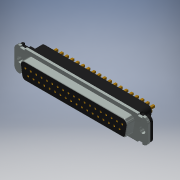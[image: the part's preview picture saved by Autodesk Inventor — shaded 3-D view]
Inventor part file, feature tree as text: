
AUTODESK INVENTOR PART (.ipt)
format: ipt  version: 2019 (Build 230136000, 136)  size: 427,520 bytes
history: native  units: mm (DEFAULTED — no unit token found)
features: extrude x12, pattern_linear x6, sketch x4, fillet x4, chamfer x1
ambient origin geometry x8: Origin, YZ Plane, XZ Plane, XY Plane, X Axis, Y Axis, Z Axis, Center Point
bodies: Solid1 (feature_tree)
feature tree (27):
  sketch  "Sketch1"  dims[d0=1.745329mm d6=0.381mm d7=2.418418mm d8=0.855895mm d9=2.418418mm]
  extrude  "Extrusion1"  Depth=0.381mm
  extrude  "Extrusion2"  Depth=1.314425mm
  fillet  "Fillet4"  Radius=1.397mm
  extrude  "Pin1"  Depth=5.08mm TaperAngle=0.0deg
  extrude  "Pin2"  Depth=5.08mm TaperAngle=0.0deg
  extrude  "Pin50"  Depth=10.4394mm
  fillet  "Fillet1"  Radius=2.794mm
  fillet  "Fillet2"  Radius=180.0mm
  fillet  "Fillet50"  Radius=2.794mm
  extrude  "Extrusion5"  Depth=1.909443mm
  extrude  "Extrusion6"  Depth=0.254mm
  sketch  "Sketch4"  dims[d24=5.08mm d25=0.0mm d26=5.08mm d27=0.0mm d28=190.0mm d30=2.794mm d31=180.0mm d33=2.794mm d34=1.909443mm d35=0.254mm d36=1.6002mm d37=0.0mm d38=5.08mm d39=0.0mm d44=0.4953mm d45=0.4953mm d46=1.016mm d52=2.8448mm d53=5.08mm d54=0.0mm d55=0.4953mm d56=5.08mm d57=0.0mm d58=0.2032mm d59=0.2032mm d60=190.0mm d62=2.794mm d63=0.381mm d67=5.1054mm d68=0.0mm d69=5.6388mm d70=0.0mm d71=5.6388mm d72=0.0mm d73=5.6388mm d74=0.0mm d75=190.0mm d77=2.794mm d78=180.0mm d80=2.794mm d81=190.0mm d83=2.794mm d86=1.909443mm d87=10.4394mm d88=57.3786mm d91=45.0deg]
  extrude  "ExtrudeSgr50"  Depth=1.6002mm TaperAngle=0.0deg
  chamfer  "Chamfer50"  Distance=5.08mm
  pattern_linear  "Pattern1"  Spacing1=0.4953mm  [1 undecoded]
  pattern_linear  "Pattern2"  Spacing1=0.4953mm  [1 undecoded]
  pattern_linear  "Pattern50"  Spacing1=1.016mm  [1 undecoded]
  extrude  "Female"  Depth=10.4394mm
  extrude  "Socket1"  Depth=5.08mm
  extrude  "Socket2"  TaperAngle=0.0deg  [1 undecoded]
  extrude  "Socket50"  Depth=0.4953mm
  pattern_linear  "Pattern5"  Spacing1=5.08mm  [1 undecoded]
  pattern_linear  "Pattern6"  Spacing1=0.0mm  [1 undecoded]
  pattern_linear  "Pattern7"  Spacing1=0.2032mm  [1 undecoded]
  sketch  "Sketch2"  dims[d11=1.314425mm d15=2.54mm d19=1.397mm]
  sketch  "Sketch3"  dims[d20=1.27mm d21=0.0mm d22=5.08mm d23=0.0mm]
note: 7 required parameter values undecoded (feature->parameter linkage not recoverable at this tier; creation-order binding heuristic only, values carry confidence <= 0.55)
